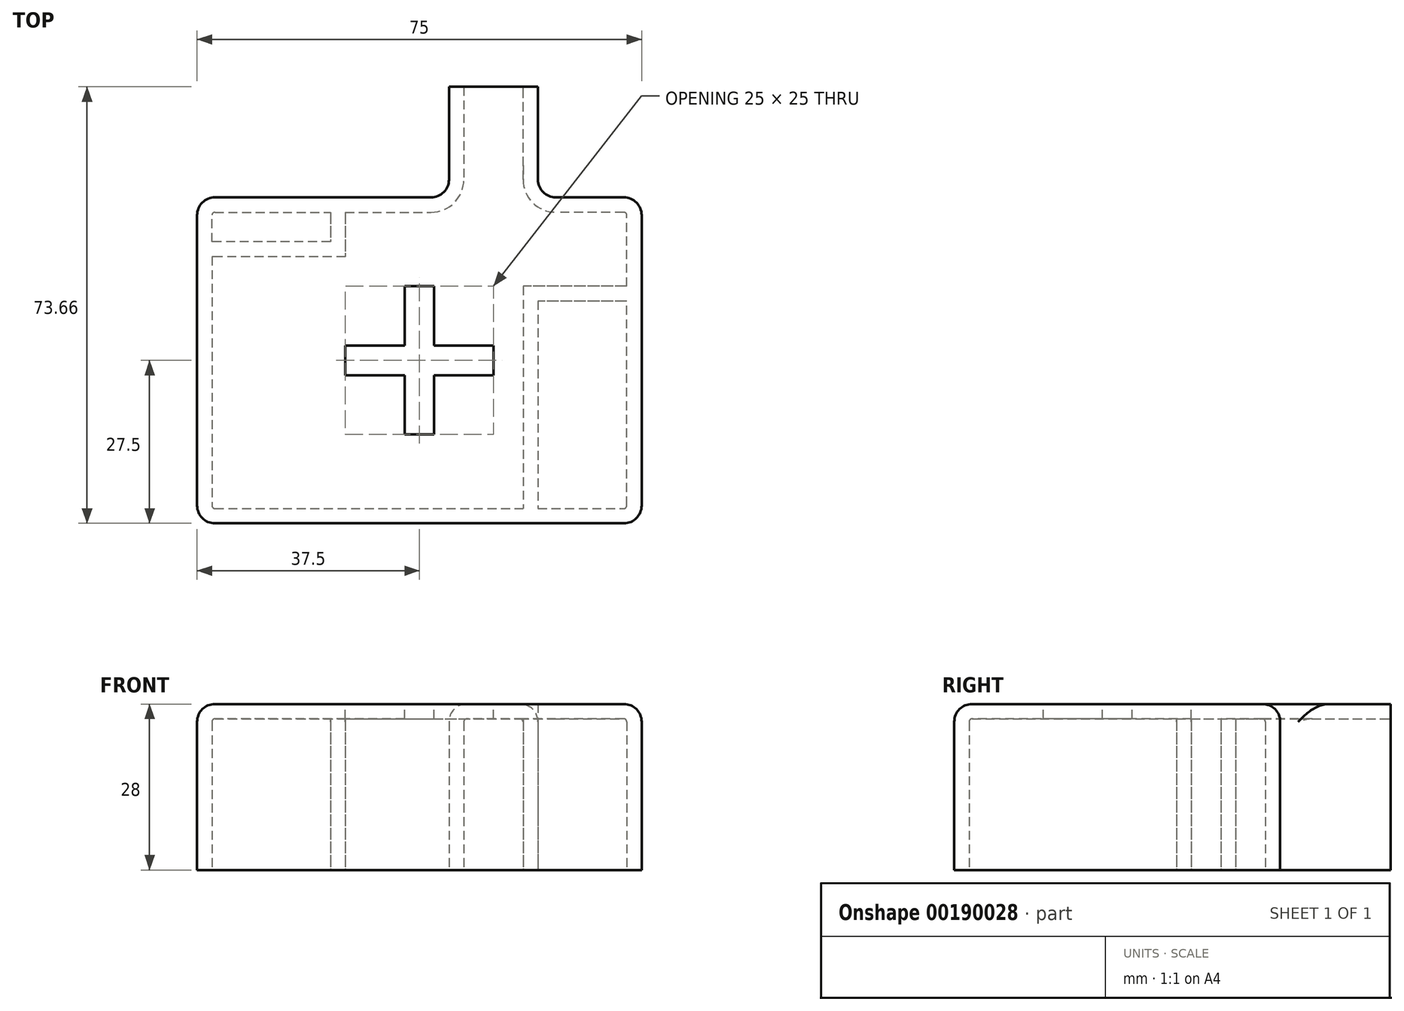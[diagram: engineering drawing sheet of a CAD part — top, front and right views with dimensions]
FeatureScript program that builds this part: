
annotation { "Feature Type Name" : "Feature", "Feature Type Description" : "" }
export const myFeature = defineFeature(function(context is Context, id is Id, definition is map)
    precondition{}
    {
        {
            var Q0;
            Q0=qCreatedBy(makeId("Top.planeOp"),FACE);
            var sketch = newSketch(context, id + "F0", { "sketchPlane" : qUnion([Q0])});
            skLineSegment(sketch, "E0", {"start": v(-37.5, -27.5) * mm, "end": v(37.5, -27.5) * mm});
            skLineSegment(sketch, "E1", {"start": v(37.5, -27.5) * mm, "end": v(37.5, 27.5) * mm});
            skLineSegment(sketch, "E2", {"start": v(37.5, 27.5) * mm, "end": v(20, 27.5) * mm});
            skLineSegment(sketch, "E3", {"start": v(-37.5, 27.5) * mm, "end": v(-37.5, -27.5) * mm});
            skLineSegment(sketch, "E4", {"start": v(20, 27.5) * mm, "end": v(20, 46.16) * mm});
            skLineSegment(sketch, "E5", {"start": v(20, 46.16) * mm, "end": v(5, 46.16) * mm});
            skLineSegment(sketch, "E6", {"start": v(5, 46.16) * mm, "end": v(5, 27.5) * mm});
            skLineSegment(sketch, "E7", {"start": v(12.5, 46.16) * mm, "end": v(12.5, 27.5) * mm, "construction": true});
            skLineSegment(sketch, "E8.trimOffspring", {"start": v(5, 27.5) * mm, "end": v(-37.5, 27.5) * mm});
            skSolve(sketch);
        }
        {
            var Q0;
            Q0=makeQuery(id+"F0.imprint","IMPRINT",FACE,{"disambiguationData":[TD([[makeQuery(id+"F0.imprint","IMPRINT",EDGE,{"derivedFrom":sQuery(id+"F0.wireOp",EDGE,"E0")}),1.0]])]});
            extrude(context, id + "F1", {"entities" : qUnion([Q0]), "depth" : 28 * mm});
        }
        {
            var Q0;
            Q0=makeQuery(id+"F1.opExtrude","CAP_EDGE",EDGE,{"disambiguationData":[OSD([sQuery(id+"F0.wireOp",EDGE,"E0")])],"isStart":false});
            var Q1;
            Q1=makeQuery(id+"F1.opExtrude","CAP_EDGE",EDGE,{"disambiguationData":[OSD([sQuery(id+"F0.wireOp",EDGE,"E1")])],"isStart":false});
            var Q2;
            Q2=makeQuery(id+"F1.opExtrude","CAP_EDGE",EDGE,{"disambiguationData":[OSD([sQuery(id+"F0.wireOp",EDGE,"E2")])],"isStart":false});
            var Q3;
            Q3=makeQuery(id+"F1.opExtrude","SWEPT_EDGE",EDGE,{"disambiguationData":[OSD([sQuery(id+"F0.wireOp",EDGE,"E1"),sQuery(id+"F0.wireOp",EDGE,"E2")])]});
            var Q4;
            Q4=makeQuery(id+"F1.opExtrude","SWEPT_EDGE",EDGE,{"disambiguationData":[OSD([sQuery(id+"F0.wireOp",EDGE,"E2"),sQuery(id+"F0.wireOp",EDGE,"E3")])]});
            var Q5;
            Q5=makeQuery(id+"F1.opExtrude","CAP_EDGE",EDGE,{"disambiguationData":[OSD([sQuery(id+"F0.wireOp",EDGE,"E3")])],"isStart":false});
            var Q6;
            Q6=makeQuery(id+"F1.opExtrude","SWEPT_EDGE",EDGE,{"disambiguationData":[OSD([sQuery(id+"F0.wireOp",EDGE,"E0"),sQuery(id+"F0.wireOp",EDGE,"E1")])]});
            var Q7;
            Q7=makeQuery(id+"F1.opExtrude","SWEPT_EDGE",EDGE,{"disambiguationData":[OSD([sQuery(id+"F0.wireOp",EDGE,"E0"),sQuery(id+"F0.wireOp",EDGE,"E3")])]});
            var Q8;
            Q8=makeQuery(id+"F1.opExtrude","CAP_EDGE",EDGE,{"disambiguationData":[OSD([sQuery(id+"F0.wireOp",EDGE,"E8.trimOffspring")])],"isStart":false});
            var Q9;
            Q9=makeQuery(id+"F1.opExtrude","CAP_EDGE",EDGE,{"disambiguationData":[OSD([sQuery(id+"F0.wireOp",EDGE,"E6")])],"isStart":false});
            var Q10;
            Q10=makeQuery(id+"F1.opExtrude","SWEPT_EDGE",EDGE,{"disambiguationData":[OSD([sQuery(id+"F0.wireOp",EDGE,"E6"),sQuery(id+"F0.wireOp",EDGE,"E8.trimOffspring")])]});
            fillet(context, id + "F2", {"entities" : qUnion([Q0, Q1, Q2, Q3, Q4, Q5, Q6, Q7, Q8, Q9, Q10]), "radius" : 3 * mm, "tangentPropagation" : true, "allowEdgeOverflow" : false});
        }
        {
            var Q0;
            Q0=makeQuery(id+"F1.opExtrude","CAP_FACE",FACE,{"disambiguationData":[OSD([sQuery(id+"F0.wireOp",EDGE,"E0"),sQuery(id+"F0.wireOp",EDGE,"E1"),sQuery(id+"F0.wireOp",EDGE,"E2"),sQuery(id+"F0.wireOp",EDGE,"E3")])],"isStart":true});
            var Q1;
            Q1=makeQuery(id+"F1.opExtrude","SWEPT_FACE",FACE,{"disambiguationData":[OSD([sQuery(id+"F0.wireOp",EDGE,"E5")])]});
            shell(context, id + "F3", {"entities" : qUnion([Q0, Q1]), "thickness" : 2.5 * mm});
        }
        {
            var Q0;
            Q0=qCreatedBy(makeId("Top.planeOp"),FACE);
            var sketch = newSketch(context, id + "F4", { "sketchPlane" : qUnion([Q0])});
            skLineSegment(sketch, "E9.0.0", {"start": v(5, 46.16) * mm, "end": v(7.5, 46.16) * mm});
            skLineSegment(sketch, "E9.0.1", {"start": v(7.5, 46.16) * mm, "end": v(7.5, 30.5) * mm});
            skArc(sketch, "E9.0.2", {"start": v(7.5, 30.5) * mm, "mid": v(5.89, 26.61) * mm, "end": v(2, 25) * mm});
            skLineSegment(sketch, "E9.0.3", {"start": v(2, 25) * mm, "end": v(-34.5, 25) * mm});
            skArc(sketch, "E9.0.4", {"start": v(-35, 24.5) * mm, "mid": v(-34.85, 24.85) * mm, "end": v(-34.5, 25) * mm});
            skLineSegment(sketch, "E9.0.5", {"start": v(-35, 24.5) * mm, "end": v(-35, -24.5) * mm});
            skArc(sketch, "E9.0.6", {"start": v(-34.5, -25) * mm, "mid": v(-34.85, -24.85) * mm, "end": v(-35, -24.5) * mm});
            skLineSegment(sketch, "E9.0.7", {"start": v(-34.5, -25) * mm, "end": v(34.5, -25) * mm});
            skArc(sketch, "E9.0.8", {"start": v(35, -24.5) * mm, "mid": v(34.85, -24.85) * mm, "end": v(34.5, -25) * mm});
            skLineSegment(sketch, "E9.0.9", {"start": v(35, -24.5) * mm, "end": v(35, 24.5) * mm});
            skArc(sketch, "E9.0.10", {"start": v(34.5, 25) * mm, "mid": v(34.85, 24.85) * mm, "end": v(35, 24.5) * mm});
            skLineSegment(sketch, "E9.0.11", {"start": v(34.5, 25) * mm, "end": v(23, 25) * mm});
            skArc(sketch, "E9.0.12", {"start": v(23, 25) * mm, "mid": v(19.11, 26.61) * mm, "end": v(17.5, 30.5) * mm});
            skLineSegment(sketch, "E9.0.13", {"start": v(17.5, 30.5) * mm, "end": v(17.5, 46.16) * mm});
            skLineSegment(sketch, "E9.0.14", {"start": v(17.5, 46.16) * mm, "end": v(20, 46.16) * mm});
            skLineSegment(sketch, "E9.0.15", {"start": v(20, 46.16) * mm, "end": v(20, 30.5) * mm});
            skArc(sketch, "E9.0.16", {"start": v(20, 30.5) * mm, "mid": v(20.88, 28.38) * mm, "end": v(23, 27.5) * mm});
            skLineSegment(sketch, "E9.0.17", {"start": v(23, 27.5) * mm, "end": v(34.5, 27.5) * mm});
            skArc(sketch, "E9.0.18", {"start": v(34.5, 27.5) * mm, "mid": v(36.62, 26.62) * mm, "end": v(37.5, 24.5) * mm});
            skLineSegment(sketch, "E9.0.19", {"start": v(37.5, 24.5) * mm, "end": v(37.5, -24.5) * mm});
            skArc(sketch, "E9.0.20", {"start": v(37.5, -24.5) * mm, "mid": v(36.62, -26.62) * mm, "end": v(34.5, -27.5) * mm});
            skLineSegment(sketch, "E9.0.21", {"start": v(34.5, -27.5) * mm, "end": v(-34.5, -27.5) * mm});
            skArc(sketch, "E9.0.22", {"start": v(-34.5, -27.5) * mm, "mid": v(-36.62, -26.62) * mm, "end": v(-37.5, -24.5) * mm});
            skLineSegment(sketch, "E9.0.23", {"start": v(-37.5, -24.5) * mm, "end": v(-37.5, 24.5) * mm});
            skArc(sketch, "E9.0.24", {"start": v(-37.5, 24.5) * mm, "mid": v(-36.62, 26.62) * mm, "end": v(-34.5, 27.5) * mm});
            skLineSegment(sketch, "E9.0.25", {"start": v(-34.5, 27.5) * mm, "end": v(2, 27.5) * mm});
            skArc(sketch, "E9.0.26", {"start": v(2, 27.5) * mm, "mid": v(4.12, 28.38) * mm, "end": v(5, 30.5) * mm});
            skLineSegment(sketch, "E9.0.27", {"start": v(5, 30.5) * mm, "end": v(5, 46.16) * mm});
            skLineSegment(sketch, "E10", {"start": v(-12.5, 25) * mm, "end": v(-12.5, 17.5) * mm});
            skLineSegment(sketch, "E11", {"start": v(-12.5, 17.5) * mm, "end": v(-35, 17.5) * mm});
            skLineSegment(sketch, "E12", {"start": v(35, 12.5) * mm, "end": v(17.5, 12.5) * mm});
            skLineSegment(sketch, "E13", {"start": v(17.5, 12.5) * mm, "end": v(17.5, -25) * mm});
            skLineSegment(sketch, "E14.0", {"start": v(-15, 20) * mm, "end": v(-35, 20) * mm});
            skLineSegment(sketch, "E14.1", {"start": v(-15, 25) * mm, "end": v(-15, 20) * mm});
            skLineSegment(sketch, "E15.0", {"start": v(20, 10) * mm, "end": v(20, -25) * mm});
            skLineSegment(sketch, "E15.1", {"start": v(35, 10) * mm, "end": v(20, 10) * mm});
            skSolve(sketch);
        }
        {
            var Q0;
            {var subQ1=sQuery(id+"F4.wireOp",EDGE,"E12");Q0=makeQuery(id+"F4.imprint","IMPRINT",FACE,{"disambiguationData":[TD([[makeQuery(id+"F4.imprint","IMPRINT",EDGE,{"derivedFrom":subQ1}),1.0]])]});}
            var Q1;
            {var subQ3=sQuery(id+"F4.wireOp",EDGE,"E10");Q1=makeQuery(id+"F4.imprint","IMPRINT",FACE,{"disambiguationData":[TD([[makeQuery(id+"F4.imprint","IMPRINT",EDGE,{"derivedFrom":subQ3}),-1.0]])]});}
            var Q2;
            Q2=makeQuery(id+"F3.opShell","OFFSET_FACE",FACE,{"disambiguationData":[OSD([sQuery(id+"F0.wireOp",EDGE,"E0"),sQuery(id+"F0.wireOp",EDGE,"E1"),sQuery(id+"F0.wireOp",EDGE,"E2"),sQuery(id+"F0.wireOp",EDGE,"E3"),sQuery(id+"F0.wireOp",EDGE,"E4"),sQuery(id+"F0.wireOp",EDGE,"E5"),sQuery(id+"F0.wireOp",EDGE,"E6"),sQuery(id+"F0.wireOp",EDGE,"E8.trimOffspring")])]});
            extrude(context, id + "F5", {"entities" : qUnion([Q0, Q1]), "operationType" : NewBodyOperationType.ADD, "endBound" : BoundingType.UP_TO_SURFACE, "endBoundEntityFace" : qUnion([Q2]), "depth" : 25 * mm});
        }
        {
            var Q0;
            Q0=makeQuery(id+"F1.opExtrude","CAP_FACE",FACE,{"disambiguationData":[OSD([sQuery(id+"F0.wireOp",EDGE,"E0"),sQuery(id+"F0.wireOp",EDGE,"E1"),sQuery(id+"F0.wireOp",EDGE,"E2"),sQuery(id+"F0.wireOp",EDGE,"E3"),sQuery(id+"F0.wireOp",EDGE,"E4"),sQuery(id+"F0.wireOp",EDGE,"E5"),sQuery(id+"F0.wireOp",EDGE,"E6"),sQuery(id+"F0.wireOp",EDGE,"E8.trimOffspring")])],"isStart":false});
            var sketch = newSketch(context, id + "F6", { "sketchPlane" : qUnion([Q0])});
            skLineSegment(sketch, "E16", {"start": v(-2.5, 12.5) * mm, "end": v(2.5, 12.5) * mm});
            skLineSegment(sketch, "E17", {"start": v(2.5, 12.5) * mm, "end": v(2.5, 2.5) * mm});
            skLineSegment(sketch, "E18", {"start": v(2.5, 2.5) * mm, "end": v(12.5, 2.5) * mm});
            skLineSegment(sketch, "E19", {"start": v(12.5, 2.5) * mm, "end": v(12.5, -2.5) * mm});
            skLineSegment(sketch, "E20", {"start": v(12.5, -2.5) * mm, "end": v(2.5, -2.5) * mm});
            skLineSegment(sketch, "E21", {"start": v(2.5, -2.5) * mm, "end": v(2.5, -12.5) * mm});
            skLineSegment(sketch, "E22", {"start": v(2.5, -12.5) * mm, "end": v(-2.5, -12.5) * mm});
            skLineSegment(sketch, "E23", {"start": v(-2.5, -12.5) * mm, "end": v(-2.5, -2.5) * mm});
            skLineSegment(sketch, "E24", {"start": v(-2.5, -2.5) * mm, "end": v(-12.5, -2.5) * mm});
            skLineSegment(sketch, "E25", {"start": v(-12.5, -2.5) * mm, "end": v(-12.5, 2.5) * mm});
            skLineSegment(sketch, "E26", {"start": v(-12.5, 2.5) * mm, "end": v(-2.5, 2.5) * mm});
            skLineSegment(sketch, "E27", {"start": v(-2.5, 2.5) * mm, "end": v(-2.5, 12.5) * mm});
            skSolve(sketch);
        }
        {
            var Q0;
            Q0=makeQuery(id+"F6.imprint","IMPRINT",FACE,{"disambiguationData":[TD([[makeQuery(id+"F6.imprint","IMPRINT",EDGE,{"derivedFrom":sQuery(id+"F6.wireOp",EDGE,"E16")}),-1.0]])]});
            var Q1;
            {var subQ0=sQuery(id+"F0.wireOp",EDGE,"E3");var subQ1=sQuery(id+"F0.wireOp",EDGE,"E0");var subQ2=sQuery(id+"F0.wireOp",EDGE,"E5");var subQ3=sQuery(id+"F0.wireOp",EDGE,"E4");var subQ4=sQuery(id+"F0.wireOp",EDGE,"E8.trimOffspring");var subQ5=sQuery(id+"F0.wireOp",EDGE,"E6");var subQ6=sQuery(id+"F0.wireOp",EDGE,"E1");var subQ7=sQuery(id+"F0.wireOp",EDGE,"E2");Q1=makeQuery(id+"F5.boolean.opBoolean","SPLIT",FACE,{"disambiguationData":[TD([makeQuery(id+"F1.opExtrude","SWEPT_FACE",FACE,{"disambiguationData":[OSD([subQ2])]})])],"derivedFrom":makeQuery(id+"F3.opShell","OFFSET_FACE",FACE,{"disambiguationData":[OSD([subQ1,subQ6,subQ7,subQ0,subQ3,subQ2,subQ5,subQ4])]})});}
            extrude(context, id + "F7", {"entities" : qUnion([Q0]), "operationType" : NewBodyOperationType.REMOVE, "endBound" : BoundingType.UP_TO_SURFACE, "oppositeDirection" : true, "endBoundEntityFace" : qUnion([Q1]), "depth" : 25 * mm});
        }
    });
